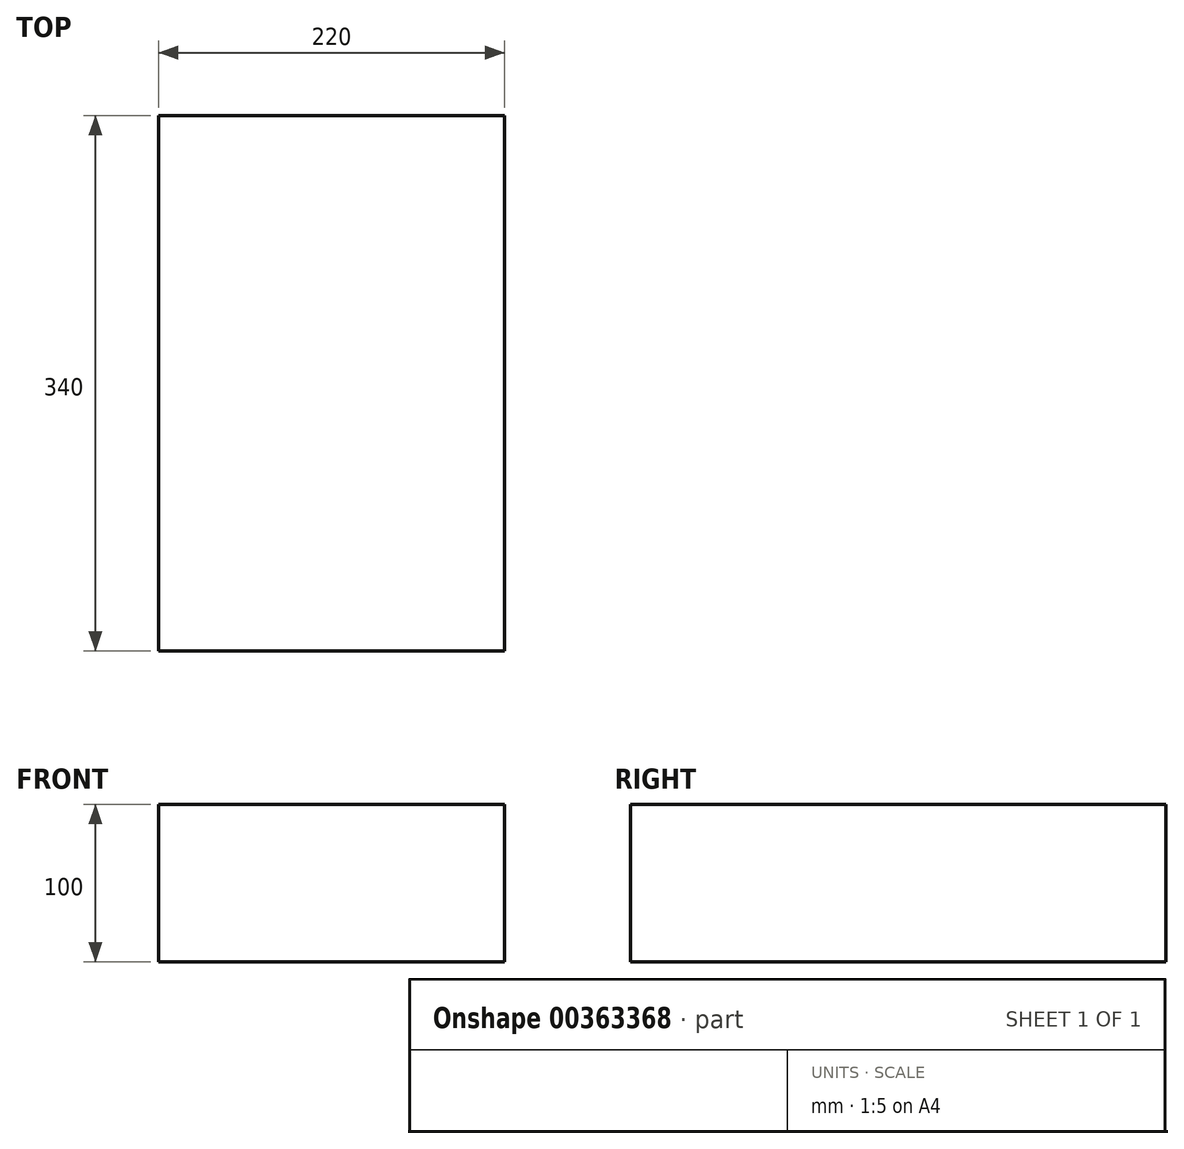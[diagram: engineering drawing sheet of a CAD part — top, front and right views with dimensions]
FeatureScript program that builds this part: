
annotation { "Feature Type Name" : "Feature", "Feature Type Description" : "" }
export const myFeature = defineFeature(function(context is Context, id is Id, definition is map)
    precondition{}
    {
        {
            var Q0;
            Q0=qCreatedBy(makeId("Top.planeOp"),FACE);
            var sketch = newSketch(context, id + "F0", { "sketchPlane" : qUnion([Q0])});
            skLineSegment(sketch, "E0.bottom", {"start": v(0, 0) * mm, "end": v(220, 0) * mm});
            skLineSegment(sketch, "E0.top", {"start": v(0, 340) * mm, "end": v(220, 340) * mm});
            skLineSegment(sketch, "E0.left", {"start": v(0, 0) * mm, "end": v(0, 340) * mm});
            skLineSegment(sketch, "E0.right", {"start": v(220, 0) * mm, "end": v(220, 340) * mm});
            skSolve(sketch);
        }
        {
            var Q0;
            Q0=makeQuery(id+"F0.imprint","IMPRINT",FACE,{"disambiguationData":[TD([[makeQuery(id+"F0.imprint","IMPRINT",EDGE,{"derivedFrom":sQuery(id+"F0.wireOp",EDGE,"E0.bottom")}),1.0]])]});
            extrude(context, id + "F1", {"entities" : qUnion([Q0]), "depth" : 100 * mm});
        }
    });
